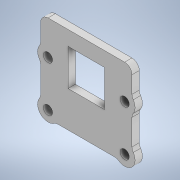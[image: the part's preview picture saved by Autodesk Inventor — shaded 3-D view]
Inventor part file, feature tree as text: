
AUTODESK INVENTOR PART (.ipt)
format: ipt  version: 2020 (Build 240168000, 168)  size: 164,864 bytes
history: native  units: in
note: dims shown in document units (in); Inventor stores cm internally (conversion verified against a paired STEP export)
features: extrude x2, fillet x2, sketch x2
ambient origin geometry x8: Origin, YZ Plane, XZ Plane, XY Plane, X Axis, Y Axis, Z Axis, Center Point
bodies: Solid1 (feature_tree)
feature tree (6):
  extrude  "Extrusion1"  Depth=0.9394in
  fillet  "Fillet1"  Radius=0.0984in
  extrude  "Extrusion2"  Depth=0.0787in
  fillet  "Fillet2"  Radius=0.5709in
  sketch  "Sketch1"  dims[d0=0.9843in d1=0.9394in d2=0.0984in]
  sketch  "Sketch2"  dims[d3=0.0787in d4=0.0787in d5=0.5709in d6=0.0787in d7=0.3937in d8=0.1575in d9=0.0787in d10=0.0in d11=0.0787in d12=0.063in d13=0.3937in d14=0.0in d15=0.0787in]
